# Revit family: Haworth_Epure_Benches_withFixedLegs_StartExtension_EU_PRELIMINARY
name_source: partatom
category: Furniture
units: mm (PartAtom-declared; Revit-internal decimal feet)

## family parameters
Always vertical = Yes
Cut with Voids When Loaded = No
OmniClass Number = 23.40.70.14.64.11
OmniClass Title = Office Furniture
Room Calculation Point = No
Shared = No
Work Plane-Based = No

## types (9) — shared parameters
Actual Height = 73 cm
Assembly Code = E2020200
Cable Tray Finish = Haworth _ Polymer _ Undecided
Description = Haworth - Epure - Benches - Bench with Fixed Legs - Start Extension
Flip Top Finish = Haworth _ Paint _ Metallic Silver
Leg Height = 70 cm
Manufacturer = Haworth
Model = EUB2LXX1X
Revision Number = 1
Size = Verify Final Dim.w/ Haworth
Trim Finish = Haworth _ Metal _ Structured White EC
URL = https://www.haworth.com
URL - Product = https://www.haworth.com
Warranty = http://www.haworth.com
Worksurface Depth = 160, 180, 200 cm
Worksurface Width = 80, 90, 100 cm

## per-type parameters (varying)
| type | Accessory Kit | Actual Depth | Actual Width | Cable Tray | Cable Tray Width | Flip Top Cable Outlet | No Accessory Kit | Round Cable Outlet |
| 80 x 160 | Yes | 160 cm | 80 cm | No | 90 cm | No | No | Yes |
| 80 x 180 | No | 180 cm | 80 cm | No | 110 cm | No | Yes | No |
| 80 x 200 | Yes | 200 cm | 80 cm | Yes | 130 cm | No | No | No |
| 90 x 160 | Yes | 160 cm | 90 cm | No | 90 cm | Yes | No | No |
| 90 x 180 | Yes | 180 cm | 90 cm | No | 110 cm | No | No | Yes |
| 90 x 200 | No | 200 cm | 90 cm | No | 130 cm | No | Yes | No |
| 100 x 160 | No | 160 cm | 100 cm | No | 90 cm | No | Yes | No |
| 100 x 180 | Yes | 180 cm | 100 cm | Yes | 110 cm | No | No | No |
| 100 x 200 | Yes | 200 cm | 100 cm | No | 130 cm | Yes | No | No |

## geometry (parser evidence)
native form markers: Blend x8, Sweep x27
no freeform markers — native parametric forms only
